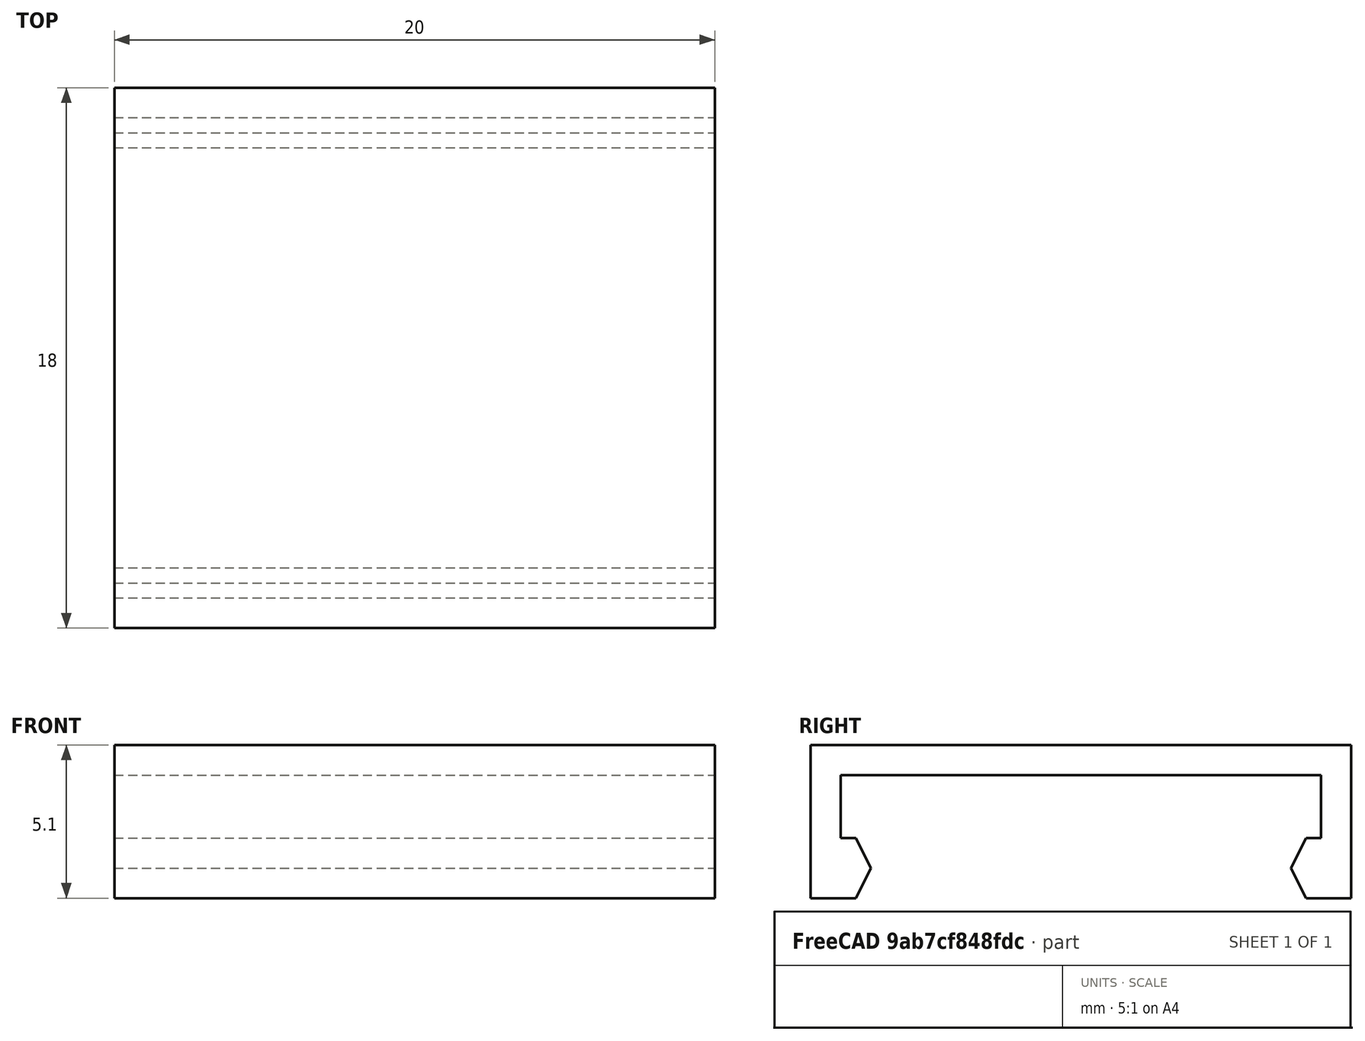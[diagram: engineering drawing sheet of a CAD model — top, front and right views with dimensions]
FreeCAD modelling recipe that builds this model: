
FCSTD DOCUMENT  (FreeCAD 0.20R29410 (Git))
Label: tapa
License: Creative Commons Attribution-ShareAlike
LicenseURL: http://creativecommons.org/licenses/by-sa/4.0/
objects: Sketcher::SketchObject×1, Part::Extrusion×1
note: 2 computed .brp shape members not serialized (recipe doc carries the construction recipe); baked Part::Feature solids carry a one-line shape summary decoded from their .brp

FEATURE [Sketcher::SketchObject] Sketch
  FullyConstrained = false
  Placement = pos=(0,0,0) rot=(0.57735,0.57735,0.57735;2.0944rad)
  sketch-geometry (16):
    g0: LineSegment StartX=-7.5 StartY=7.9 StartZ=0 EndX=-7 EndY=6.9 EndZ=0
    g1: LineSegment StartX=-7 StartY=6.9 StartZ=0 EndX=-7.5 EndY=5.9 EndZ=0
    g2: LineSegment StartX=-7.5 StartY=5.9 StartZ=0 EndX=-9 EndY=5.9 EndZ=0
    g3: LineSegment StartX=-9 StartY=5.9 StartZ=0 EndX=-9 EndY=11 EndZ=0
    g4: LineSegment StartX=-9 StartY=11 StartZ=0 EndX=0 EndY=11 EndZ=0
    g5: LineSegment StartX=-7.5 StartY=7.9 StartZ=0 EndX=-8 EndY=7.9 EndZ=0
    g6: LineSegment StartX=-8 StartY=7.9 StartZ=0 EndX=-8 EndY=10 EndZ=0
    g7: LineSegment StartX=-8 StartY=10 StartZ=0 EndX=0 EndY=10 EndZ=0
    g8: LineSegment StartX=7.5 StartY=7.9 StartZ=0 EndX=7 EndY=6.9 EndZ=0
    g9: LineSegment StartX=7 StartY=6.9 StartZ=0 EndX=7.5 EndY=5.9 EndZ=0
    g10: LineSegment StartX=7.5 StartY=5.9 StartZ=0 EndX=9 EndY=5.9 EndZ=0
    g11: LineSegment StartX=9 StartY=5.9 StartZ=0 EndX=9 EndY=11 EndZ=0
    g12: LineSegment StartX=9 StartY=11 StartZ=0 EndX=0 EndY=11 EndZ=0
    g13: LineSegment StartX=7.5 StartY=7.9 StartZ=0 EndX=8 EndY=7.9 EndZ=0
    g14: LineSegment StartX=8 StartY=7.9 StartZ=0 EndX=8 EndY=10 EndZ=0
    g15: LineSegment StartX=8 StartY=10 StartZ=0 EndX=0 EndY=10 EndZ=0
  constraints (41):
    c: Coincident(g0,g1)
    c: Coincident(g1,g2)
    c: Horizontal(g2)
    c: Coincident(g2,g3)
    c: Vertical(g3)
    c: Coincident(g3,g4)
    c: Horizontal(g4)
    c: PointOnObject(g4,g-2)
    c: Coincident(g0,g5)
    c: Horizontal(g5)
    c: Coincident(g5,g6)
    c: Vertical(g6)
    c: Coincident(g6,g7)
    c: PointOnObject(g7,g-2)
    c: Horizontal(g7)
    c: Distance(g5,g2) = 2
    c: DistanceX(g5,g0) = 1
    c: DistanceX(g2,g2) = 1.5
    c: DistanceY(g6,g6) = 2.1
    c: Distance(g6,g3) = 1
    c: Distance(g6,g4) = 1
    c: DistanceX(g5,g0) = 0.5
    c: DistanceY(g1,g0) = 1
    c: Distance(g-1,g7) = 10
    c: DistanceX(g3,g4) = 9
    c: Coincident(g8,g9)
    c: Coincident(g9,g10)
    c: Horizontal(g10)
    c: Coincident(g10,g11)
    c: Vertical(g11)
    c: Coincident(g11,g12)
    c: Horizontal(g12)
    c: Coincident(g8,g13)
    c: Horizontal(g13)
    c: Coincident(g13,g14)
    c: Vertical(g14)
    c: Coincident(g14,g15)
    c: Horizontal(g15)
    c: Distance(g13,g10) = 2
    c: Distance(g14,g11) = 1
    c: Distance(g14,g12) = 1
FEATURE [Part::Extrusion] Extrude
  Base = -> Sketch
  Dir = (1,0,0)
  DirMode = 2
  FaceMakerClass = Part::FaceMakerBullseye
  LengthFwd = 20
  LengthRev = 0
  Solid = true
  Symmetric = false
